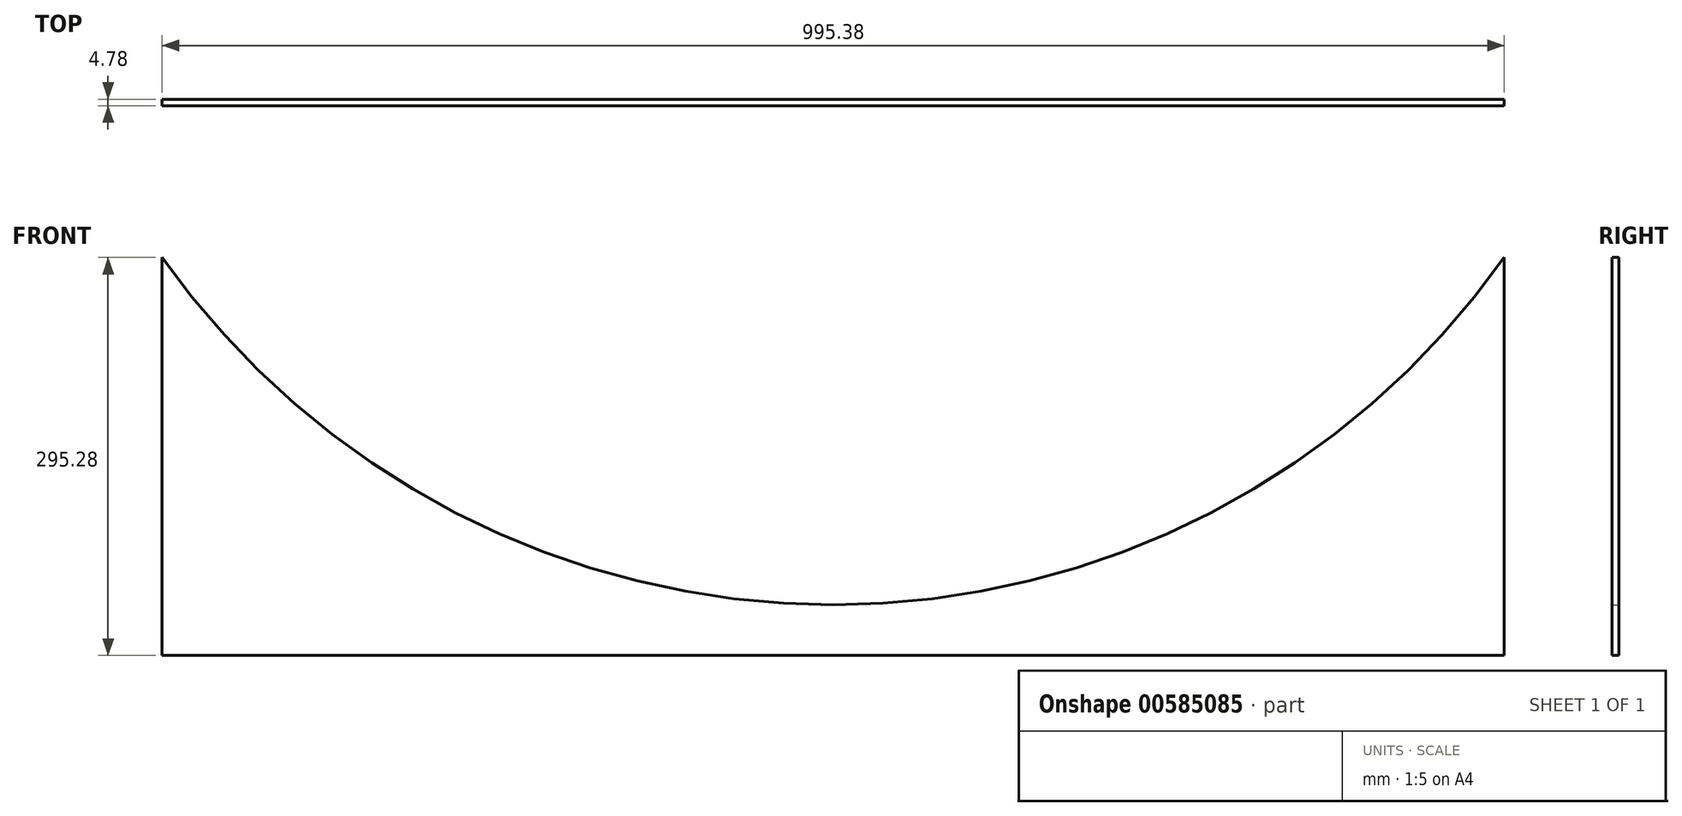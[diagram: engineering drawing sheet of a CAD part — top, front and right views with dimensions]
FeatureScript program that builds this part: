
annotation { "Feature Type Name" : "Feature", "Feature Type Description" : "" }
export const myFeature = defineFeature(function(context is Context, id is Id, definition is map)
    precondition{}
    {
        {
            var Q0;
            Q0=qCreatedBy(makeId("Front.planeOp"),FACE);
            var sketch = newSketch(context, id + "F0", { "sketchPlane" : qUnion([Q0])});
            skLineSegment(sketch, "E0", {"start": v(995.38, 0) * mm, "end": v(995.38, 295.27) * mm});
            skLineSegment(sketch, "E1", {"start": v(0, 0) * mm, "end": v(0, 295.28) * mm});
            skArc(sketch, "E2", {"start": v(0, 295.27) * mm, "mid": v(497.69, 37.7) * mm, "end": v(995.38, 295.28) * mm});
            skLineSegment(sketch, "E3", {"start": v(0, 0) * mm, "end": v(995.38, 0) * mm});
            skSolve(sketch);
        }
        {
            var Q0;
            Q0=makeQuery(id+"F0.imprint","IMPRINT",FACE,{"disambiguationData":[TD([[makeQuery(id+"F0.imprint","IMPRINT",EDGE,{"derivedFrom":sQuery(id+"F0.wireOp",EDGE,"E0")}),1.0]])]});
            extrude(context, id + "F1", {"entities" : qUnion([Q0]), "depth" : 4.78 * mm, "offsetDistance" : 25.4 * mm});
        }
    });
